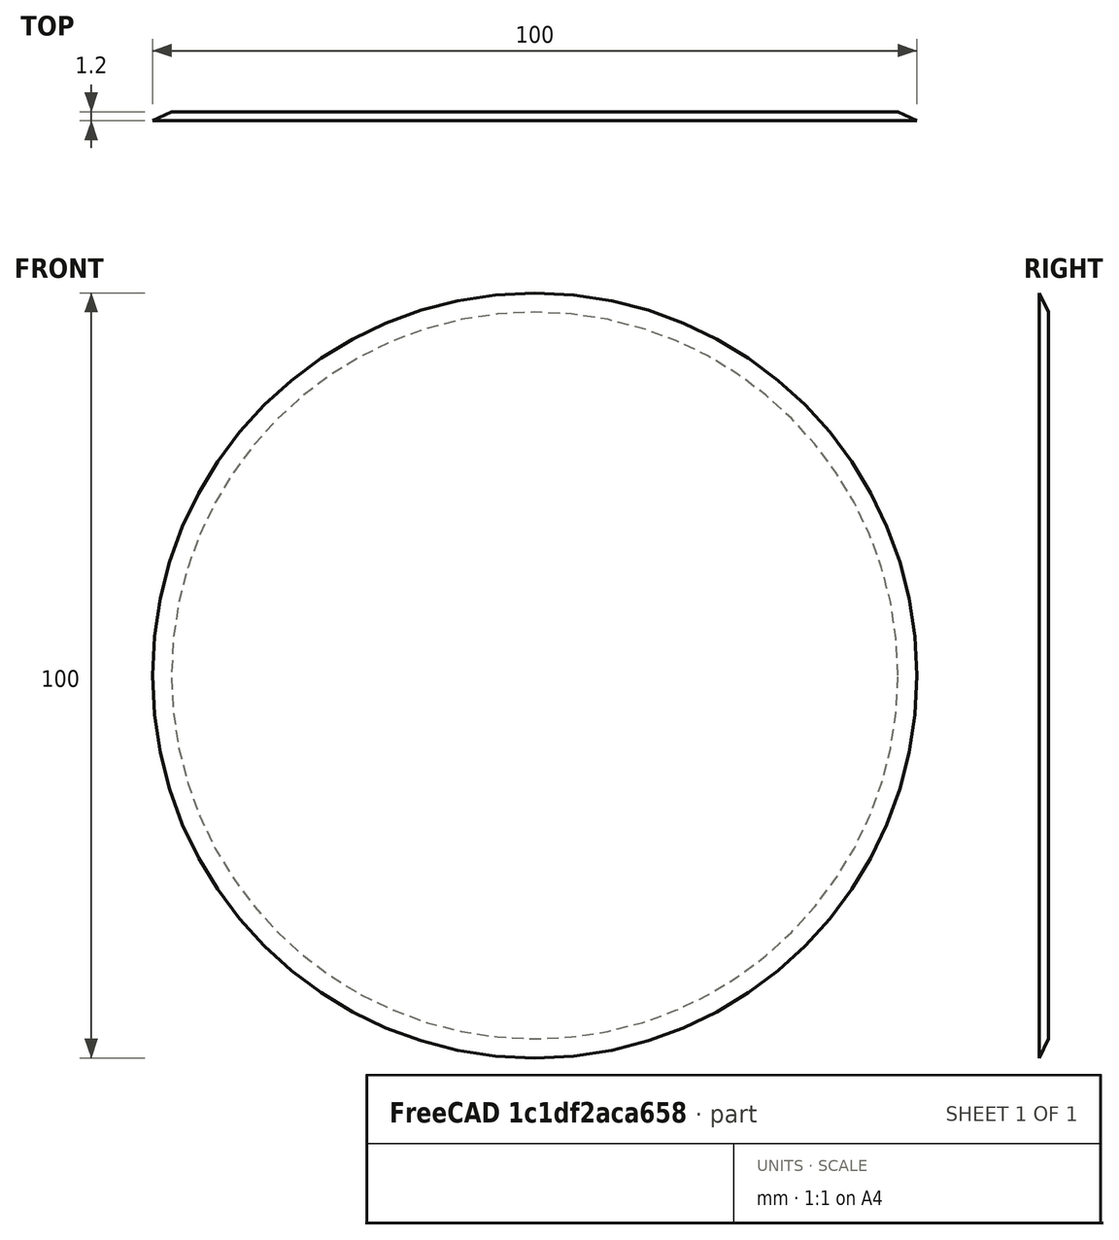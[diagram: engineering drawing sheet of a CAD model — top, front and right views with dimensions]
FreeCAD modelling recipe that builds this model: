
FCSTD DOCUMENT  (FreeCAD 0.21R32532 (Git))
Label: RS-100_R
License: All rights reserved
LicenseURL: http://en.wikipedia.org/wiki/All_rights_reserved
objects: PartDesign::CoordinateSystem×2, Sketcher::SketchObject×1, PartDesign::Revolution×1, PartDesign::Body×1
note: 6 computed .brp shape members not serialized (recipe doc carries the construction recipe); baked Part::Feature solids carry a one-line shape summary decoded from their .brp

FEATURE [Sketcher::SketchObject] Sketch
  FullyConstrained = true
  MapMode = 5
  Placement = pos=(0,0,0) rot=(0.57735,0.57735,0.57735;2.0944rad)
  Support = -> [YZ_Plane]
  sketch-geometry (4):
    g0: LineSegment StartX=0 StartY=0 StartZ=0 EndX=1.2 EndY=0 EndZ=0
    g1: LineSegment StartX=1.2 StartY=0 StartZ=0 EndX=1.2 EndY=47.5 EndZ=0
    g2: LineSegment StartX=1.2 StartY=47.5 StartZ=0 EndX=0 EndY=50 EndZ=0
    g3: LineSegment StartX=0 StartY=50 StartZ=0 EndX=0 EndY=0 EndZ=0
  constraints (11):
    c: Coincident(g-1,g0)
    c: PointOnObject(g0,g-1)
    c: Coincident(g0,g1)
    c: Vertical(g1)
    c: Coincident(g1,g2)
    c: PointOnObject(g2,g-2)
    c: Coincident(g2,g3)
    c: Coincident(g3,g0)
    c: DistanceX(g0) = 1.2  'width'
    c: DistanceY(g2) = 50  'r'
    c: DistanceY(g1,g2) = 2.5
FEATURE [PartDesign::Revolution] Revolution
  Angle = 360
  Axis = (3e-16,1,-2e-16)
  Base = (0,0,0)
  Placement = pos=(0,0,0) rot=(0.57735,0.57735,0.57735;2.0944rad)
  Profile = -> Sketch
  ReferenceAxis = -> Sketch [H_Axis]
FEATURE [PartDesign::CoordinateSystem] Local_CS  label="front"
  AttacherType = Attacher::AttachEngine3D
  MapMode = 5
  Placement = pos=(0,0,0) rot=(1,0,0;1.5708rad)
  Support = -> [XZ_Plane]
FEATURE [PartDesign::CoordinateSystem] Local_CS001  label="back"
  AttacherType = Attacher::AttachEngine3D
  AttachmentOffset = pos=(0,0,1.2) rot=(0,0,1;0rad)
  MapMode = 5
  Placement = pos=(0,1.2,3e-16) rot=(0,0.707107,0.707107;3.14159rad)
  Support = -> [XZ_Plane]
  expr: .AttachmentOffset.Base.z = Sketch.Constraints.width
FEATURE [PartDesign::Body] Body  label="rs_100_r"
  Group = -> [Sketch,Revolution,Local_CS,Local_CS001]
  Origin = -> Origin
  Tip = -> Revolution
